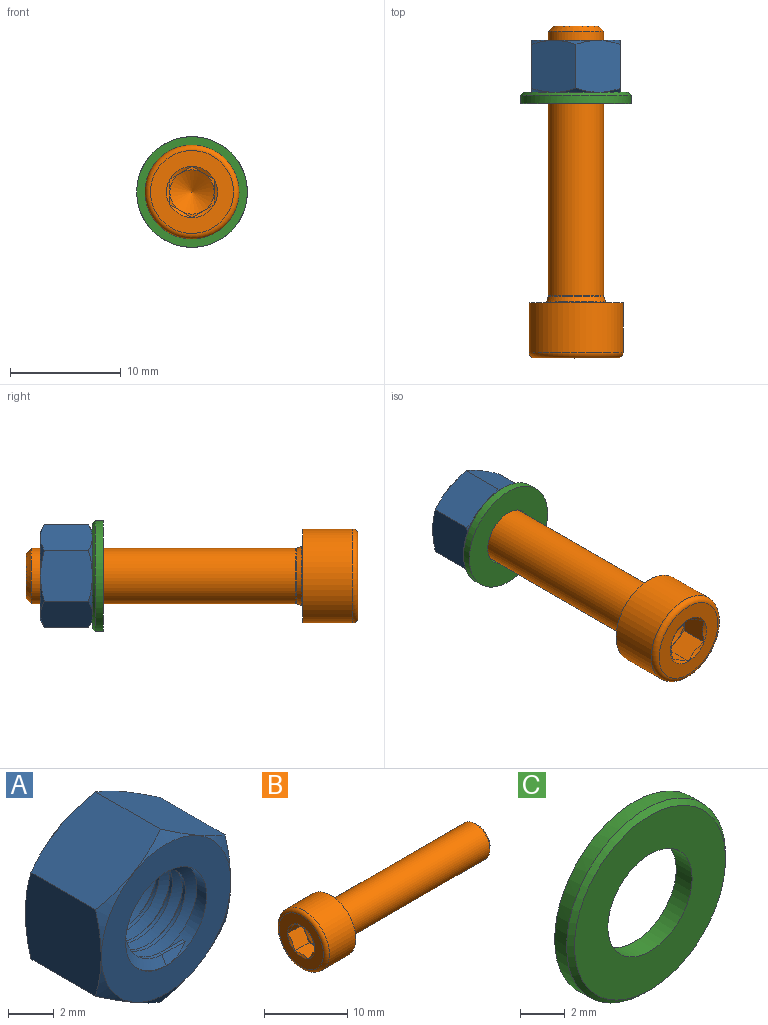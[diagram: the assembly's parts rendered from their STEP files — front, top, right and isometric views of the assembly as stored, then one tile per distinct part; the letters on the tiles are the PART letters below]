
ASSEMBLY  parts=3 mates=2
PART A: 18 faces, bbox 9.4x4.8x9.4 mm
  f0: plane 7.99x7.99mm, normal (0,-1,0), area 30.5mm2, adj f2,f11
  f1: plane 7.99x7.99mm, normal (0,1,0), area 30.5mm2, adj f2,f10
  f2: cylinder r=2.5mm len=5mm, axis (0,1,0), area 18mm2, adj f0,f1,f3,f5,f6,f7,f8,f9
  f3: plane 0.7x0.46mm, normal (-1,0,-0.03), area 0.2mm2, adj f2,f4,f5,f6
  f4: cylinder r=2.04mm len=4.17mm, axis (0,1,0), area 11.3mm2, adj f3,f5,f6,f7
  f5: bspline ~5.77x5mm, area 37.6mm2, adj f2,f3,f4,f8
  f6: bspline ~5.77x5mm, area 37.6mm2, adj f2,f3,f4,f9
  f7: plane 1.44x0.18mm, normal (0,0,1), area 0.3mm2, adj f2,f4,f8,f9
  f8: plane 1.57x0.59mm, normal (0,0.87,0.5), area 0.5mm2, adj f2,f5,f7
  f9: plane 1.57x0.59mm, normal (0,-0.87,0.5), area 0.5mm2, adj f2,f6,f7
  f10: cone r=3.99mm half-angle=60deg, axis (0,-1,0), area 6.1mm2, adj f1,f12,f13,f14,f15,f16,f17
  f11: cone r=4.62mm half-angle=60deg, axis (0,1,0), area 6.1mm2, adj f0,f12,f13,f14,f15,f16,f17
  f12: plane 4.7x4mm, normal (-0.5,0,0.87), area 20.5mm2, adj f10,f11,f13,f17
  f13: plane 4.7x4mm, normal (0.5,0,0.87), area 20.5mm2, adj f10,f11,f12,f14
  f14: plane 4.69x4.62mm, normal (1,0,0), area 20.5mm2, adj f10,f11,f13,f15
  f15: plane 4.7x4mm, normal (0.5,0,-0.87), area 20.5mm2, adj f10,f11,f14,f16
  f16: plane 4.7x4mm, normal (-0.5,0,-0.87), area 20.5mm2, adj f10,f11,f15,f17
  f17: plane 4.69x4.62mm, normal (-1,0,0), area 20.5mm2, adj f10,f11,f12,f16
PART B: 24 faces, bbox 30x9.2x9.2 mm
  f0: plane 1.73x1mm, normal (-1,0,0), area 0.2mm2, adj f16,f17,f23
  f1: plane 2x0.58mm, normal (-1,0,0), area 0.2mm2, adj f17,f18,f23
  f2: plane 1.73x1mm, normal (-1,0,0), area 0.2mm2, adj f18,f19,f23
  f3: plane 1.73x1mm, normal (-1,0,0), area 0.2mm2, adj f19,f20,f23
  f4: plane 2x0.58mm, normal (-1,0,0), area 0.2mm2, adj f20,f21,f23
  f5: cone r=2.31mm half-angle=60deg, axis (-1,0,0), area 3.4mm2, adj f15,f16,f17,f18,f19,f20,f21
  f6: cone r=2.51mm half-angle=20.6deg, axis (-1,0,0), area 6.9mm2, adj f7,f11
  f7: torus R=2.7mm, axis (1,0,0), area 1.1mm2, adj f6,f10
  f8: plane 4.02x4.02mm, normal (1,0,0), area 12.7mm2, adj f9
  f9: cone r=2.5mm half-angle=45deg, axis (-1,0,0), area 9.8mm2, adj f8,f10
  f10: cylinder r=2.5mm len=23.91mm, axis (1,0,0), area 375.6mm2, adj f7,f9
  f11: torus R=2.85mm, axis (1,0,0), area 4.2mm2, adj f6,f13
  f12: cylinder r=4.25mm len=8.5mm, axis (1,0,0), area 120.2mm2, adj f13,f14
  f13: plane 8.5x8.5mm, normal (1,0,0), area 31.2mm2, adj f11,f12
  f14: torus R=3.75mm, axis (1,0,0), area 20.1mm2, adj f12,f15
  f15: plane 7.5x7.5mm, normal (-1,0,0), area 27.4mm2, adj f5,f14
  f16: plane 2.5x2.31mm, normal (0,0,-1), area 5.5mm2, adj f0,f5,f17,f21,f22
  f17: plane 2.5x2mm, normal (0,0.87,-0.5), area 5.5mm2, adj f0,f1,f5,f16,f18
  f18: plane 2.5x2mm, normal (0,0.87,0.5), area 5.5mm2, adj f1,f2,f5,f17,f19
  f19: plane 2.5x2.31mm, normal (0,0,1), area 5.5mm2, adj f2,f3,f5,f18,f20
  f20: plane 2.5x2mm, normal (0,-0.87,0.5), area 5.5mm2, adj f3,f4,f5,f19,f21
  f21: plane 2.5x2mm, normal (0,-0.87,-0.5), area 5.5mm2, adj f4,f5,f16,f20,f22
  f22: plane 1.73x1mm, normal (-1,0,0), area 0.2mm2, adj f16,f21,f23
  f23: cone r=2mm half-angle=60deg, axis (-1,0,0), area 14.5mm2, adj f0,f1,f2,f3,f4,f22
PART C: 5 faces, bbox 10x1x10 mm
  f0: cylinder r=2.65mm len=5.3mm, axis (0,1,0), area 16.7mm2, adj f2,f3
  f1: cylinder r=5mm len=10mm, axis (0,1,0), area 23.6mm2, adj f3,f4
  f2: plane 9.5x9.5mm, normal (0,-1,0), area 48.8mm2, adj f0,f4
  f3: plane 10x10mm, normal (0,1,0), area 56.5mm2, adj f0,f1
  f4: cone r=5mm half-angle=45deg, axis (0,1,0), area 10.8mm2, adj f1,f2
PLACE A t=(2.46,18.92,3.31)mm
PLACE B rot(axis=(-0.58,-0.58,0.58),120deg) t=(2.46,-4.78,3.31)mm fixed
PLACE C rot(axis=(1,0,0),180deg) t=(2.46,13.22,3.31)mm
MATE fastened C.f0 <-> B.f5  axis (0,-1,0) through (2.46,13.22,3.31)mm
MATE fastened A.f2 <-> C.f0  axis (0,-1,0) through (2.46,14.22,3.31)mm
